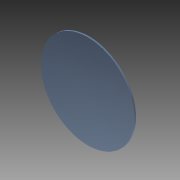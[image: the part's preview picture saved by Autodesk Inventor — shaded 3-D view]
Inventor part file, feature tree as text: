
AUTODESK INVENTOR PART (.ipt)
format: ipt  version: 2015 (Build 190159000, 159)  size: 86,528 bytes
history: native  units: mm
features: other x1, revolve x1, sketch x1
ambient origin geometry x8: Origin, YZ Plane, XZ Plane, XY Plane, X Axis, Y Axis, Z Axis, Center Point
bodies: Body1 (feature_tree)
feature tree (3):
  other  "Sólido1"
  revolve  "Revolución1"  [1 undecoded]
  sketch  "Boceto1"  dims[d0=63.5mm d1=2.0mm d2=6.0mm d3=10000.0mm d4=90.0deg]
note: 1 required parameter value undecoded (feature->parameter linkage not recoverable at this tier; creation-order binding heuristic only, values carry confidence <= 0.55)
